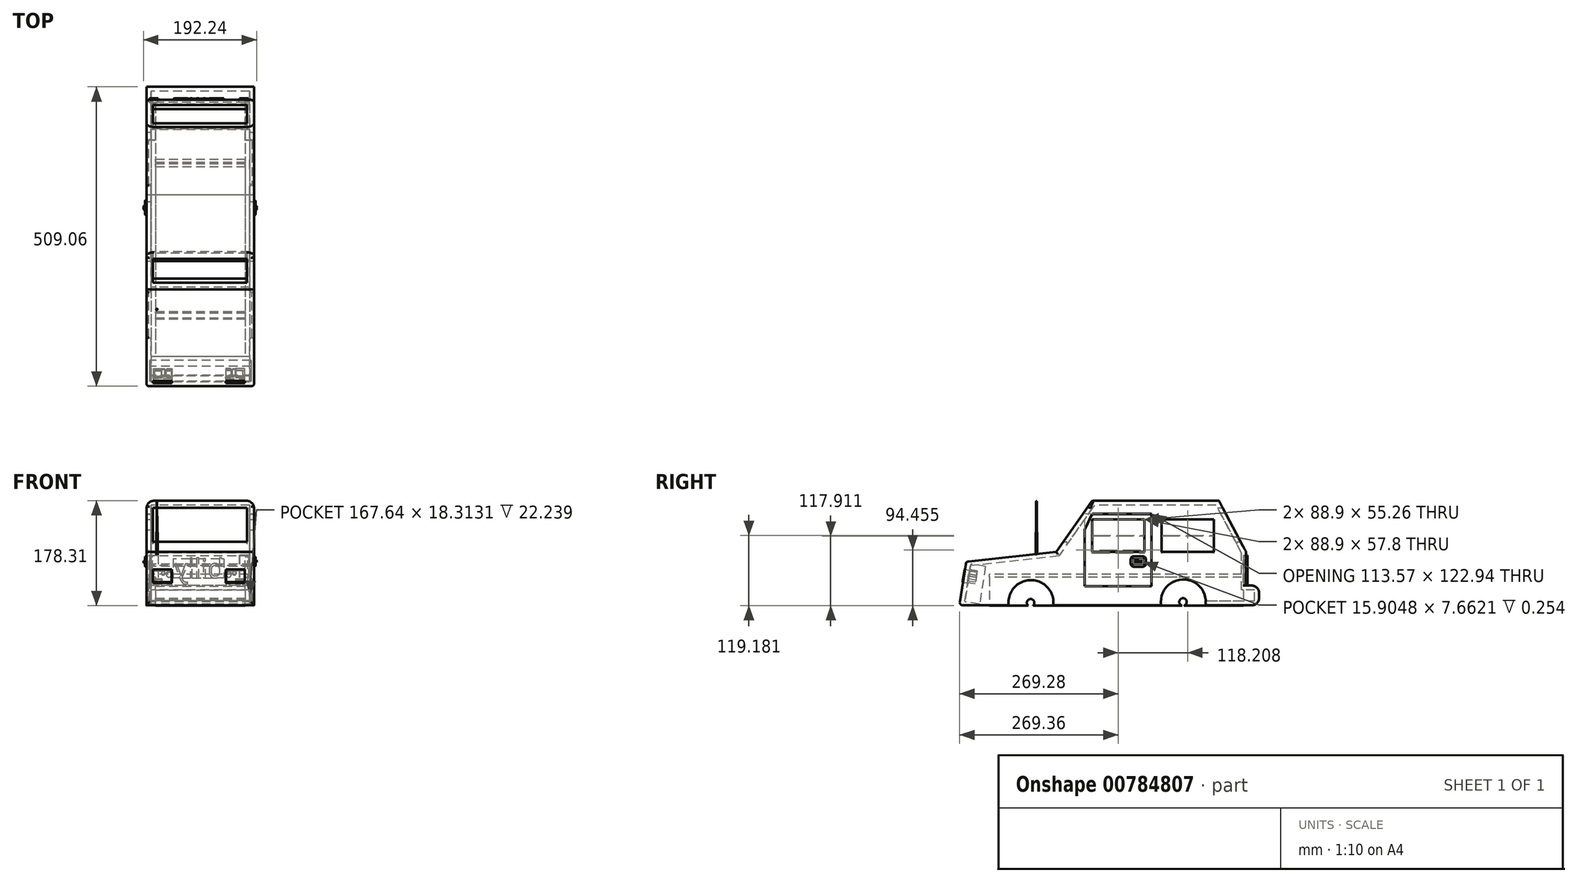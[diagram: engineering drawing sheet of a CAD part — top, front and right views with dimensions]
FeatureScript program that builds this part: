
annotation { "Feature Type Name" : "Feature", "Feature Type Description" : "" }
export const myFeature = defineFeature(function(context is Context, id is Id, definition is map)
    precondition{}
    {
        {
            var Q0;
            Q0=qCreatedBy(makeId("Right.planeOp"),FACE);
            var sketch = newSketch(context, id + "F0", { "sketchPlane" : qUnion([Q0])});
            skLineSegment(sketch, "E0", {"start": v(-225.77, -91.04) * mm, "end": v(261.9, -91.04) * mm});
            skLineSegment(sketch, "E1", {"start": v(261.9, 0) * mm, "end": v(215.84, 86.76) * mm});
            skLineSegment(sketch, "E2", {"start": v(215.84, 86.76) * mm, "end": v(0, 86.76) * mm});
            skLineSegment(sketch, "E3", {"start": v(0, 86.76) * mm, "end": v(-60.74, 0) * mm});
            skLineSegment(sketch, "E4", {"start": v(-60.74, 0) * mm, "end": v(-214.13, -17) * mm});
            skLineSegment(sketch, "E5", {"start": v(-214.13, -17) * mm, "end": v(-225.77, -91.04) * mm});
            skLineSegment(sketch, "E6", {"start": v(261.9, -91.04) * mm, "end": v(261.9, -183.2) * mm});
            skLineSegment(sketch, "E7", {"start": v(261.9, -183.2) * mm, "end": v(139.99, -183.2) * mm});
            skLineSegment(sketch, "E8", {"start": v(-225.77, -91.04) * mm, "end": v(-225.77, -187.69) * mm});
            skLineSegment(sketch, "E9", {"start": v(-225.77, -187.69) * mm, "end": v(-103.85, -187.69) * mm});
            skCircle(sketch, "E10", {"center": v(-103.85, -86.57) * mm, "radius": 38.1 * mm});
            skCircle(sketch, "E11", {"center": v(155.31, -85.2) * mm, "radius": 38.1 * mm});
            skLineSegment(sketch, "E12", {"start": v(261.9, -91.04) * mm, "end": v(284.15, -91.04) * mm});
            skLineSegment(sketch, "E13", {"start": v(284.15, -91.04) * mm, "end": v(284.15, -57.49) * mm});
            skLineSegment(sketch, "E14", {"start": v(284.15, -57.49) * mm, "end": v(261.9, -57.49) * mm});
            skLineSegment(sketch, "E15", {"start": v(261.9, -57.49) * mm, "end": v(261.9, 0) * mm});
            skCircle(sketch, "E16", {"center": v(-103.85, -86.57) * mm, "radius": 6.35 * mm});
            skCircle(sketch, "E17", {"center": v(155.31, -85.2) * mm, "radius": 6.35 * mm});
            skSolve(sketch);
        }
        {
            var Q0;
            Q0=makeQuery(id+"F0.imprint","IMPRINT",FACE,{"disambiguationData":[TD([[makeQuery(id+"F0.imprint","IMPRINT",EDGE,{"derivedFrom":sQuery(id+"F0.wireOp",EDGE,"E1")}),1.0]])]});
            extrude(context, id + "F1", {"entities" : qUnion([Q0]), "depth" : 182.88 * mm, "offsetDistance" : 25.4 * mm});
        }
        {
            var Q0;
            Q0=makeQuery(id+"F1.opExtrude","SWEPT_BODY",BODY,{"disambiguationData":[OSD([sQuery(id+"F0.wireOp",EDGE,"E0"),sQuery(id+"F0.wireOp",EDGE,"QMBNyazt-kVT2-uFLO-qqQZ-oCFPkPWxmDB5"),sQuery(id+"F0.wireOp",EDGE,"E1"),sQuery(id+"F0.wireOp",EDGE,"E2"),sQuery(id+"F0.wireOp",EDGE,"E3"),sQuery(id+"F0.wireOp",EDGE,"E4"),sQuery(id+"F0.wireOp",EDGE,"E5"),sQuery(id+"F0.wireOp",EDGE,"E10"),sQuery(id+"F0.wireOp",EDGE,"E11")])]});
            transform(context, id + "F2", {"entities" : qUnion([Q0]), "transformType" : TransformType.TRANSLATION_3D, "dx" : -88.9 * mm, "dy" : 0 * mm, "dz" : 0 * mm, "makeCopy" : false});
        }
        {
            var Q0;
            {var subQ0=sQuery(id+"F0.wireOp",EDGE,"E0");Q0=makeQuery(id+"F1.opExtrude","SWEPT_FACE",FACE,{"disambiguationData":[OSD([subQ0]),TDD([makeQuery(id+"F0.imprint","IMPRINT",EDGE,{"disambiguationData":[TD([[makeQuery(id+"F0.imprint","INTERSECT",VERTEX,{"disambiguationData":[OD(1.0)],"derivedFrom":[subQ0,sQuery(id+"F0.wireOp",EDGE,"E10")]}),-1.0]])],"derivedFrom":subQ0})])]});}
            var Q1;
            {var subQ0=sQuery(id+"F0.wireOp",EDGE,"E0");Q1=makeQuery(id+"F1.opExtrude","SWEPT_FACE",FACE,{"disambiguationData":[OSD([subQ0]),TDD([makeQuery(id+"F0.imprint","IMPRINT",EDGE,{"disambiguationData":[TD([[makeQuery(id+"F0.imprint","INTERSECT",VERTEX,{"derivedFrom":[subQ0,sQuery(id+"F0.wireOp",EDGE,"QMBNyazt-kVT2-uFLO-qqQZ-oCFPkPWxmDB5")]}),1.0]])],"derivedFrom":subQ0})])]});}
            var Q2;
            {var subQ0=sQuery(id+"F0.wireOp",EDGE,"E0");Q2=makeQuery(id+"F1.opExtrude","SWEPT_FACE",FACE,{"disambiguationData":[OSD([subQ0]),TDD([makeQuery(id+"F0.imprint","IMPRINT",EDGE,{"disambiguationData":[TD([[makeQuery(id+"F0.imprint","INTERSECT",VERTEX,{"derivedFrom":[subQ0,sQuery(id+"F0.wireOp",EDGE,"E5")]}),-1.0]])],"derivedFrom":subQ0})])]});}
            var Q3;
            Q3=makeQuery(id+"F1.opExtrude","SWEPT_FACE",FACE,{"disambiguationData":[OSD([sQuery(id+"F0.wireOp",EDGE,"E10")])]});
            var Q4;
            Q4=makeQuery(id+"F1.opExtrude","SWEPT_FACE",FACE,{"disambiguationData":[OSD([sQuery(id+"F0.wireOp",EDGE,"E11")])]});
            shell(context, id + "F3", {"entities" : qUnion([Q0, Q1, Q2, Q3, Q4]), "thickness" : 7.62 * mm});
        }
        {
            var Q0;
            Q0=makeQuery(id+"F1.opExtrude","CAP_EDGE",EDGE,{"disambiguationData":[OSD([sQuery(id+"F0.wireOp",EDGE,"E2")])],"isStart":false});
            var Q1;
            Q1=makeQuery(id+"F1.opExtrude","CAP_EDGE",EDGE,{"disambiguationData":[OSD([sQuery(id+"F0.wireOp",EDGE,"E2")])],"isStart":true});
            var Q2;
            Q2=makeQuery(id+"F1.opExtrude","SWEPT_EDGE",EDGE,{"disambiguationData":[OSD([sQuery(id+"F0.wireOp",EDGE,"E13"),sQuery(id+"F0.wireOp",EDGE,"E14")])]});
            var Q3;
            Q3=makeQuery(id+"F1.opExtrude","SWEPT_EDGE",EDGE,{"disambiguationData":[OSD([sQuery(id+"F0.wireOp",EDGE,"E12"),sQuery(id+"F0.wireOp",EDGE,"E13")])]});
            fillet(context, id + "F4", {"entities" : qUnion([Q0, Q1, Q2, Q3]), "radius" : 12.7 * mm, "tangentPropagation" : true, "allowEdgeOverflow" : false});
        }
        {
            var Q0;
            Q0=makeQuery(id+"F1.opExtrude","CAP_FACE",FACE,{"disambiguationData":[OSD([sQuery(id+"F0.wireOp",EDGE,"E0"),sQuery(id+"F0.wireOp",EDGE,"QMBNyazt-kVT2-uFLO-qqQZ-oCFPkPWxmDB5"),sQuery(id+"F0.wireOp",EDGE,"E1"),sQuery(id+"F0.wireOp",EDGE,"E2"),sQuery(id+"F0.wireOp",EDGE,"E3"),sQuery(id+"F0.wireOp",EDGE,"E4"),sQuery(id+"F0.wireOp",EDGE,"E5"),sQuery(id+"F0.wireOp",EDGE,"E10"),sQuery(id+"F0.wireOp",EDGE,"E11")])],"isStart":false});
            var sketch = newSketch(context, id + "F5", { "sketchPlane" : qUnion([Q0])});
            skLineSegment(sketch, "E18.bottom", {"start": v(0, 55.26) * mm, "end": v(88.9, 55.26) * mm});
            skLineSegment(sketch, "E18.top", {"start": v(0, 0) * mm, "end": v(88.9, 0) * mm});
            skLineSegment(sketch, "E18.left", {"start": v(0, 55.26) * mm, "end": v(0, 0) * mm});
            skLineSegment(sketch, "E18.right", {"start": v(88.9, 55.26) * mm, "end": v(88.9, 0) * mm});
            skLineSegment(sketch, "E19.bottom", {"start": v(207.1, 55.26) * mm, "end": v(118.2, 55.26) * mm});
            skLineSegment(sketch, "E19.top", {"start": v(207.1, 0) * mm, "end": v(118.2, 0) * mm});
            skLineSegment(sketch, "E19.left", {"start": v(207.1, 55.26) * mm, "end": v(207.1, 0) * mm});
            skLineSegment(sketch, "E19.right", {"start": v(118.2, 55.26) * mm, "end": v(118.2, 0) * mm});
            skSolve(sketch);
        }
        {
            var Q0;
            Q0 = qSketchRegion(id + "F5", true);
            extrude(context, id + "F6", {"entities" : qUnion([Q0]), "operationType" : NewBodyOperationType.REMOVE, "oppositeDirection" : true, "depth" : 182.88 * mm, "offsetDistance" : 25.4 * mm});
        }
        {
            var Q0;
            Q0=makeQuery(id+"F1.opExtrude","SWEPT_FACE",FACE,{"disambiguationData":[OSD([sQuery(id+"F0.wireOp",EDGE,"E15")])]});
            var sketch = newSketch(context, id + "F7", { "sketchPlane" : qUnion([Q0])});
            skLineSegment(sketch, "E20.bottom", {"start": v(-82.2, 74.99) * mm, "end": v(77.83, 74.99) * mm});
            skLineSegment(sketch, "E20.top", {"start": v(-82.2, 16.87) * mm, "end": v(77.83, 16.87) * mm});
            skLineSegment(sketch, "E20.left", {"start": v(-82.2, 74.99) * mm, "end": v(-82.2, 16.87) * mm});
            skLineSegment(sketch, "E20.right", {"start": v(77.83, 74.99) * mm, "end": v(77.83, 16.87) * mm});
            skSolve(sketch);
        }
        {
            var Q0;
            Q0 = qSketchRegion(id + "F7", true);
            extrude(context, id + "F8", {"entities" : qUnion([Q0]), "operationType" : NewBodyOperationType.REMOVE, "oppositeDirection" : true, "depth" : 487.68 * mm, "offsetDistance" : 25.4 * mm});
        }
        {
            var Q0;
            Q0=makeQuery(id+"F1.opExtrude","CAP_EDGE",EDGE,{"disambiguationData":[OSD([sQuery(id+"F0.wireOp",EDGE,"E4")])],"isStart":false});
            var Q1;
            Q1=makeQuery(id+"F1.opExtrude","CAP_EDGE",EDGE,{"disambiguationData":[OSD([sQuery(id+"F0.wireOp",EDGE,"E3")])],"isStart":false});
            var Q2;
            Q2=makeQuery(id+"F1.opExtrude","CAP_EDGE",EDGE,{"disambiguationData":[OSD([sQuery(id+"F0.wireOp",EDGE,"E4")])],"isStart":true});
            var Q3;
            Q3=makeQuery(id+"F1.opExtrude","SWEPT_EDGE",EDGE,{"disambiguationData":[OSD([sQuery(id+"F0.wireOp",EDGE,"E4"),sQuery(id+"F0.wireOp",EDGE,"E5")])]});
            var Q4;
            Q4=makeQuery(id+"F1.opExtrude","CAP_EDGE",EDGE,{"disambiguationData":[OSD([sQuery(id+"F0.wireOp",EDGE,"E5")])],"isStart":true});
            var Q5;
            Q5=makeQuery(id+"F1.opExtrude","SWEPT_EDGE",EDGE,{"disambiguationData":[OSD([sQuery(id+"F0.wireOp",EDGE,"E0"),sQuery(id+"F0.wireOp",EDGE,"E5")])]});
            var Q6;
            Q6=makeQuery(id+"F1.opExtrude","CAP_EDGE",EDGE,{"disambiguationData":[OSD([sQuery(id+"F0.wireOp",EDGE,"E5")])],"isStart":false});
            fillet(context, id + "F9", {"entities" : qUnion([Q0, Q1, Q2, Q3, Q4, Q5, Q6]), "radius" : 5.08 * mm, "tangentPropagation" : true, "allowEdgeOverflow" : false});
        }
        {
            var Q0;
            Q0=makeQuery(id+"F1.opExtrude","SWEPT_EDGE",EDGE,{"disambiguationData":[OSD([sQuery(id+"F0.wireOp",EDGE,"E1"),sQuery(id+"F0.wireOp",EDGE,"E15")])]});
            var Q1;
            Q1=makeQuery(id+"F1.opExtrude","CAP_EDGE",EDGE,{"disambiguationData":[OSD([sQuery(id+"F0.wireOp",EDGE,"E15")])],"isStart":false});
            var Q2;
            Q2=makeQuery(id+"F1.opExtrude","CAP_EDGE",EDGE,{"disambiguationData":[OSD([sQuery(id+"F0.wireOp",EDGE,"E15")])],"isStart":true});
            var Q3;
            Q3=makeQuery(id+"F1.opExtrude","CAP_EDGE",EDGE,{"disambiguationData":[OSD([sQuery(id+"F0.wireOp",EDGE,"E11")])],"isStart":true});
            var Q4;
            {var subQ0=sQuery(id+"F0.wireOp",EDGE,"E11");Q4=makeQuery(id+"F3.opShell","OFFSET_EDGE",EDGE,{"disambiguationData":[OSD([subQ0]),TDD([makeQuery(id+"F1.opExtrude","CAP_EDGE",EDGE,{"disambiguationData":[OSD([subQ0])],"isStart":true})])]});}
            var Q5;
            Q5=makeQuery(id+"F1.opExtrude","CAP_EDGE",EDGE,{"disambiguationData":[OSD([sQuery(id+"F0.wireOp",EDGE,"E10")])],"isStart":true});
            var Q6;
            {var subQ0=sQuery(id+"F0.wireOp",EDGE,"E10");Q6=makeQuery(id+"F3.opShell","OFFSET_EDGE",EDGE,{"disambiguationData":[OSD([subQ0]),TDD([makeQuery(id+"F1.opExtrude","CAP_EDGE",EDGE,{"disambiguationData":[OSD([subQ0])],"isStart":true})])]});}
            var Q7;
            {var subQ0=sQuery(id+"F0.wireOp",EDGE,"E10");Q7=makeQuery(id+"F3.opShell","OFFSET_EDGE",EDGE,{"disambiguationData":[OSD([subQ0]),TDD([makeQuery(id+"F1.opExtrude","CAP_EDGE",EDGE,{"disambiguationData":[OSD([subQ0])],"isStart":false})])]});}
            var Q8;
            Q8=makeQuery(id+"F1.opExtrude","CAP_EDGE",EDGE,{"disambiguationData":[OSD([sQuery(id+"F0.wireOp",EDGE,"E10")])],"isStart":false});
            var Q9;
            Q9=makeQuery(id+"F1.opExtrude","CAP_EDGE",EDGE,{"disambiguationData":[OSD([sQuery(id+"F0.wireOp",EDGE,"E11")])],"isStart":false});
            var Q10;
            {var subQ0=sQuery(id+"F0.wireOp",EDGE,"E11");Q10=makeQuery(id+"F3.opShell","OFFSET_EDGE",EDGE,{"disambiguationData":[OSD([subQ0]),TDD([makeQuery(id+"F1.opExtrude","CAP_EDGE",EDGE,{"disambiguationData":[OSD([subQ0])],"isStart":false})])]});}
            fillet(context, id + "F10", {"entities" : qUnion([Q0, Q1, Q2, Q3, Q4, Q5, Q6, Q7, Q8, Q9, Q10]), "radius" : 5.08 * mm, "tangentPropagation" : true, "allowEdgeOverflow" : false});
        }
        {
            var Q0;
            Q0=makeQuery(id+"F1.opExtrude","SWEPT_FACE",FACE,{"disambiguationData":[OSD([sQuery(id+"F0.wireOp",EDGE,"E2")])]});
            var sketch = newSketch(context, id + "F11", { "sketchPlane" : qUnion([Q0])});
            skLineSegment(sketch, "E21.bottom", {"start": v(-72.8, 259.2) * mm, "end": v(79.6, 259.2) * mm});
            skLineSegment(sketch, "E21.top", {"start": v(-72.8, -172.6) * mm, "end": v(79.6, -172.6) * mm});
            skLineSegment(sketch, "E21.left", {"start": v(-72.8, 259.2) * mm, "end": v(-72.8, -172.6) * mm});
            skLineSegment(sketch, "E21.right", {"start": v(79.6, 259.2) * mm, "end": v(79.6, -172.6) * mm});
            skSolve(sketch);
        }
        {
            var Q0;
            Q0 = qSketchRegion(id + "F11", true);
            extrude(context, id + "F12", {"entities" : qUnion([Q0]), "depth" : 48.26 * mm, "offsetDistance" : 25.4 * mm});
        }
        {
            var Q0;
            Q0=makeQuery(id+"F12.opExtrude","SWEPT_BODY",BODY,{"disambiguationData":[OSD([sQuery(id+"F11.wireOp",EDGE,"E21.bottom"),sQuery(id+"F11.wireOp",EDGE,"E21.top"),sQuery(id+"F11.wireOp",EDGE,"E21.left"),sQuery(id+"F11.wireOp",EDGE,"E21.right")])]});
            transform(context, id + "F13", {"entities" : qUnion([Q0]), "transformType" : TransformType.TRANSLATION_3D, "dx" : -0.76 * mm, "dy" : -1.78 * mm, "dz" : -178.3 * mm, "makeCopy" : false});
        }
        {
            var Q0;
            Q0=makeQuery(id+"F12.opExtrude","SWEPT_FACE",FACE,{"disambiguationData":[OSD([sQuery(id+"F11.wireOp",EDGE,"E21.right")])]});
            var sketch = newSketch(context, id + "F14", { "sketchPlane" : qUnion([Q0])});
            skCircle(sketch, "E22", {"center": v(-104.4, -86.72) * mm, "radius": 6.35 * mm});
            skCircle(sketch, "E23", {"center": v(154.77, -85.35) * mm, "radius": 6.35 * mm});
            skSolve(sketch);
        }
        {
            var Q0;
            Q0 = qSketchRegion(id + "F14", true);
            extrude(context, id + "F15", {"entities" : qUnion([Q0]), "operationType" : NewBodyOperationType.REMOVE, "oppositeDirection" : true, "depth" : 154.94 * mm, "offsetDistance" : 25.4 * mm});
        }
        {
            var Q0;
            Q0=makeQuery(id+"F1.opExtrude","CAP_FACE",FACE,{"disambiguationData":[OSD([sQuery(id+"F0.wireOp",EDGE,"E0"),sQuery(id+"F0.wireOp",EDGE,"E1"),sQuery(id+"F0.wireOp",EDGE,"E2"),sQuery(id+"F0.wireOp",EDGE,"E3"),sQuery(id+"F0.wireOp",EDGE,"E4"),sQuery(id+"F0.wireOp",EDGE,"E5"),sQuery(id+"F0.wireOp",EDGE,"E10"),sQuery(id+"F0.wireOp",EDGE,"E11"),sQuery(id+"F0.wireOp",EDGE,"E12"),sQuery(id+"F0.wireOp",EDGE,"E13"),sQuery(id+"F0.wireOp",EDGE,"E14"),sQuery(id+"F0.wireOp",EDGE,"E15")])],"isStart":false});
            var sketch = newSketch(context, id + "F16", { "sketchPlane" : qUnion([Q0])});
            skLineSegment(sketch, "E24", {"start": v(101.15, 64.38) * mm, "end": v(0, 64.38) * mm});
            skLineSegment(sketch, "E25", {"start": v(101.15, 64.38) * mm, "end": v(101.15, -58.57) * mm});
            skLineSegment(sketch, "E26", {"start": v(101.15, -58.57) * mm, "end": v(-12.41, -58.57) * mm});
            skLineSegment(sketch, "E27", {"start": v(-12.41, -58.57) * mm, "end": v(-12.41, 37.02) * mm});
            skLineSegment(sketch, "E28", {"start": v(-12.41, 37.02) * mm, "end": v(0, 64.38) * mm});
            skPoint(sketch, "E29.endSnap0", {"position": v(118.2, 27.63) * mm});
            skPoint(sketch, "E30", {"position": v(88.9, 27.63) * mm});
            skLineSegment(sketch, "E31", {"start": v(100.88, -58.3) * mm, "end": v(-12.3, -58.3) * mm});
            skLineSegment(sketch, "E32", {"start": v(-12.3, -58.3) * mm, "end": v(-12.3, 37) * mm});
            skLineSegment(sketch, "E33", {"start": v(-12.3, 37) * mm, "end": v(0.08, 64.26) * mm});
            skLineSegment(sketch, "E34", {"start": v(0.08, 64.26) * mm, "end": v(101.02, 64.26) * mm});
            skLineSegment(sketch, "E35", {"start": v(101.02, 64.26) * mm, "end": v(100.88, -58.3) * mm});
            skSolve(sketch);
        }
        {
            var Q0;
            Q0=makeQuery(id+"F12.opExtrude","CAP_FACE",FACE,{"disambiguationData":[OSD([sQuery(id+"F11.wireOp",EDGE,"E21.bottom"),sQuery(id+"F11.wireOp",EDGE,"E21.top"),sQuery(id+"F11.wireOp",EDGE,"E21.left"),sQuery(id+"F11.wireOp",EDGE,"E21.right")])],"isStart":false});
            var sketch = newSketch(context, id + "F17", { "sketchPlane" : qUnion([Q0])});
            skLineSegment(sketch, "E36.bottom", {"start": v(-83.73, 257.43) * mm, "end": v(91.53, 257.43) * mm});
            skLineSegment(sketch, "E36.top", {"start": v(-83.73, -174.37) * mm, "end": v(91.53, -174.37) * mm});
            skLineSegment(sketch, "E36.left", {"start": v(-83.73, 257.43) * mm, "end": v(-83.73, -174.37) * mm});
            skLineSegment(sketch, "E37", {"start": v(91.53, 257.43) * mm, "end": v(91.53, -174.37) * mm});
            skSolve(sketch);
        }
        {
            var Q0;
            Q0 = qSketchRegion(id + "F17", true);
            extrude(context, id + "F18", {"entities" : qUnion([Q0]), "operationType" : NewBodyOperationType.ADD, "depth" : 5.08 * mm, "offsetDistance" : 25.4 * mm});
        }
        {
            var Q0;
            Q0=qCreatedBy(makeId("Top.planeOp"),FACE);
            var sketch = newSketch(context, id + "F19", { "sketchPlane" : qUnion([Q0])});
            skCircle(sketch, "E38", {"center": v(-71.2, -94.38) * mm, "radius": 1.14 * mm});
            skSolve(sketch);
        }
        {
            var Q0;
            Q0 = qSketchRegion(id + "F19", true);
            extrude(context, id + "F20", {"entities" : qUnion([Q0]), "depth" : 38.1 * mm, "offsetDistance" : 25.4 * mm});
        }
        {
            var Q0;
            Q0=makeQuery(id+"F20.opExtrude","SWEPT_BODY",BODY,{"disambiguationData":[OSD([sQuery(id+"F19.wireOp",EDGE,"E38")])]});
            transform(context, id + "F21", {"entities" : qUnion([Q0]), "transformType" : TransformType.TRANSLATION_3D, "dx" : 0 * mm, "dy" : 0 * mm, "dz" : -5.08 * mm, "makeCopy" : false});
        }
        {
            var Q0;
            Q0=makeQuery(id+"F20.opExtrude","CAP_FACE",FACE,{"disambiguationData":[OSD([sQuery(id+"F19.wireOp",EDGE,"E38")])],"isStart":false});
            var sketch = newSketch(context, id + "F22", { "sketchPlane" : qUnion([Q0])});
            skCircle(sketch, "E39", {"center": v(-71.2, -94.38) * mm, "radius": 0.76 * mm});
            skSolve(sketch);
        }
        {
            var Q0;
            Q0 = qSketchRegion(id + "F22", true);
            extrude(context, id + "F23", {"entities" : qUnion([Q0]), "operationType" : NewBodyOperationType.ADD, "depth" : 27.7 * mm, "offsetDistance" : 25.4 * mm});
        }
        {
            var Q0;
            Q0=makeQuery(id+"F23.opExtrude","CAP_FACE",FACE,{"disambiguationData":[OSD([sQuery(id+"F22.wireOp",EDGE,"E39")])],"isStart":false});
            var sketch = newSketch(context, id + "F24", { "sketchPlane" : qUnion([Q0])});
            skCircle(sketch, "E40", {"center": v(-71.2, -94.38) * mm, "radius": 0.45 * mm});
            skSolve(sketch);
        }
        {
            var Q0;
            Q0 = qSketchRegion(id + "F24", true);
            extrude(context, id + "F25", {"entities" : qUnion([Q0]), "operationType" : NewBodyOperationType.ADD, "depth" : 25.4 * mm, "offsetDistance" : 25.4 * mm});
        }
        {
            var Q0;
            Q0 = qSketchRegion(id + "F16", true);
            extrude(context, id + "F26", {"entities" : qUnion([Q0]), "operationType" : NewBodyOperationType.REMOVE, "oppositeDirection" : true, "depth" : 185.42 * mm, "offsetDistance" : 25.4 * mm});
        }
        {
            var Q0;
            {var subQ0=sQuery(id+"F0.wireOp",EDGE,"E15");var subQ1=sQuery(id+"F0.wireOp",EDGE,"E14");var subQ2=sQuery(id+"F0.wireOp",EDGE,"E13");var subQ3=sQuery(id+"F0.wireOp",EDGE,"E12");var subQ4=sQuery(id+"F0.wireOp",EDGE,"E11");var subQ5=sQuery(id+"F0.wireOp",EDGE,"E10");var subQ6=sQuery(id+"F0.wireOp",EDGE,"E5");var subQ7=sQuery(id+"F0.wireOp",EDGE,"E4");var subQ8=sQuery(id+"F0.wireOp",EDGE,"E3");var subQ9=sQuery(id+"F0.wireOp",EDGE,"E2");var subQ10=sQuery(id+"F0.wireOp",EDGE,"E1");var subQ11=sQuery(id+"F0.wireOp",EDGE,"E0");var subQ12=makeQuery(id+"F1.opExtrude","CAP_FACE",FACE,{"disambiguationData":[OSD([subQ11,subQ10,subQ9,subQ8,subQ7,subQ6,subQ5,subQ4,subQ3,subQ2,subQ1,subQ0])],"isStart":false});Q0=makeQuery(id+"F26.boolean.opBoolean","SPLIT",FACE,{"disambiguationData":[TD([makeQuery(id+"F26.opExtrude","SWEPT_FACE",FACE,{"disambiguationData":[OSD([sQuery(id+"F16.wireOp",EDGE,"E31")])]})])],"derivedFrom":subQ12});}
            var sketch = newSketch(context, id + "F27", { "sketchPlane" : qUnion([Q0])});
            skLineSegment(sketch, "E41", {"start": v(27.11, -12.7) * mm, "end": v(27.11, -20.37) * mm});
            skLineSegment(sketch, "E42", {"start": v(70.73, -7.8) * mm, "end": v(86.64, -7.8) * mm});
            skLineSegment(sketch, "E43", {"start": v(70.73, -25.3) * mm, "end": v(86.64, -25.3) * mm});
            skLineSegment(sketch, "E44", {"start": v(30.88, -12.7) * mm, "end": v(30.88, -20.37) * mm});
            skLineSegment(sketch, "E45", {"start": v(70.73, -12.7) * mm, "end": v(70.73, -20.37) * mm});
            skLineSegment(sketch, "E46", {"start": v(86.64, -12.7) * mm, "end": v(86.64, -20.37) * mm});
            skArc(sketch, "E47", {"start": v(70.73, -7.8) * mm, "mid": v(67.27, -9.24) * mm, "end": v(65.83, -12.7) * mm});
            skArc(sketch, "E48", {"start": v(70.73, -25.3) * mm, "mid": v(67.25, -23.85) * mm, "end": v(65.8, -20.37) * mm});
            skArc(sketch, "E49", {"start": v(86.64, -25.3) * mm, "mid": v(90.12, -23.85) * mm, "end": v(91.56, -20.37) * mm});
            skArc(sketch, "E50", {"start": v(86.64, -7.8) * mm, "mid": v(90.1, -9.24) * mm, "end": v(91.54, -12.7) * mm});
            skLineSegment(sketch, "E51", {"start": v(65.83, -12.7) * mm, "end": v(65.8, -20.37) * mm});
            skLineSegment(sketch, "E52", {"start": v(91.54, -12.7) * mm, "end": v(91.56, -20.37) * mm});
            skLineSegment(sketch, "E53", {"start": v(70.73, -20.37) * mm, "end": v(86.64, -20.37) * mm});
            skLineSegment(sketch, "E54", {"start": v(70.73, -12.7) * mm, "end": v(86.64, -12.7) * mm});
            skSolve(sketch);
        }
        {
            var Q0;
            Q0 = qSketchRegion(id + "F27", true);
            extrude(context, id + "F28", {"entities" : qUnion([Q0]), "operationType" : NewBodyOperationType.ADD, "depth" : 2.54 * mm, "offsetDistance" : 25.4 * mm});
        }
        {
            var Q0;
            Q0=makeQuery(id+"F28.opExtrude","CAP_FACE",FACE,{"disambiguationData":[OSD([sQuery(id+"F27.wireOp",EDGE,"E42"),sQuery(id+"F27.wireOp",EDGE,"E43"),sQuery(id+"F27.wireOp",EDGE,"E45"),sQuery(id+"F27.wireOp",EDGE,"E46"),sQuery(id+"F27.wireOp",EDGE,"E47"),sQuery(id+"F27.wireOp",EDGE,"E48"),sQuery(id+"F27.wireOp",EDGE,"E49"),sQuery(id+"F27.wireOp",EDGE,"E50"),sQuery(id+"F27.wireOp",EDGE,"E51"),sQuery(id+"F27.wireOp",EDGE,"E52"),sQuery(id+"F27.wireOp",EDGE,"E53"),sQuery(id+"F27.wireOp",EDGE,"E54")])],"isStart":false});
            var Q1;
            Q1=makeQuery(id+"F28.opExtrude","CAP_EDGE",EDGE,{"disambiguationData":[OSD([sQuery(id+"F27.wireOp",EDGE,"E43")])],"isStart":false});
            var Q2;
            Q2=makeQuery(id+"F28.opExtrude","CAP_EDGE",EDGE,{"disambiguationData":[OSD([sQuery(id+"F27.wireOp",EDGE,"E51")])],"isStart":false});
            var Q3;
            Q3=makeQuery(id+"F28.opExtrude","CAP_EDGE",EDGE,{"disambiguationData":[OSD([sQuery(id+"F27.wireOp",EDGE,"E42")])],"isStart":false});
            var Q4;
            Q4=makeQuery(id+"F28.opExtrude","CAP_EDGE",EDGE,{"disambiguationData":[OSD([sQuery(id+"F27.wireOp",EDGE,"E52")])],"isStart":false});
            var Q5;
            Q5=makeQuery(id+"F28.opExtrude","CAP_EDGE",EDGE,{"disambiguationData":[OSD([sQuery(id+"F27.wireOp",EDGE,"E45")])],"isStart":false});
            var Q6;
            Q6=makeQuery(id+"F28.opExtrude","CAP_EDGE",EDGE,{"disambiguationData":[OSD([sQuery(id+"F27.wireOp",EDGE,"E53")])],"isStart":false});
            var Q7;
            Q7=makeQuery(id+"F28.opExtrude","CAP_EDGE",EDGE,{"disambiguationData":[OSD([sQuery(id+"F27.wireOp",EDGE,"E46")])],"isStart":false});
            var Q8;
            Q8=makeQuery(id+"F28.opExtrude","CAP_EDGE",EDGE,{"disambiguationData":[OSD([sQuery(id+"F27.wireOp",EDGE,"E54")])],"isStart":false});
            fillet(context, id + "F29", {"entities" : qUnion([Q0, Q1, Q2, Q3, Q4, Q5, Q6, Q7, Q8]), "radius" : 2.3 * mm, "tangentPropagation" : true, "allowEdgeOverflow" : false});
        }
        {
            var Q0;
            {var subQ0=sQuery(id+"F11.wireOp",EDGE,"E21.left");var subQ1=sQuery(id+"F11.wireOp",EDGE,"E21.right");Q0=makeQuery(id+"F15.boolean.opBoolean","SPLIT",FACE,{"disambiguationData":[TD([makeQuery(id+"F12.opExtrude","SWEPT_FACE",FACE,{"disambiguationData":[OSD([subQ0])]}),makeQuery(id+"F12.opExtrude","SWEPT_FACE",FACE,{"disambiguationData":[OSD([subQ1])]}),makeQuery(id+"F15.opExtrude","SWEPT_FACE",FACE,{"disambiguationData":[OSD([sQuery(id+"F14.wireOp",EDGE,"E22")])]}),makeQuery(id+"F15.opExtrude","SWEPT_FACE",FACE,{"disambiguationData":[OSD([sQuery(id+"F14.wireOp",EDGE,"E23")])]})])],"derivedFrom":makeQuery(id+"F12.opExtrude","CAP_FACE",FACE,{"disambiguationData":[OSD([sQuery(id+"F11.wireOp",EDGE,"E21.bottom"),sQuery(id+"F11.wireOp",EDGE,"E21.top"),subQ0,subQ1])],"isStart":true})});}
            var sketch = newSketch(context, id + "F30", { "sketchPlane" : qUnion([Q0])});
            skLineSegment(sketch, "E55", {"start": v(94.06, -71.15) * mm, "end": v(98.34, -73.34) * mm});
            skLineSegment(sketch, "E56", {"start": v(98.34, -73.34) * mm, "end": v(98.34, -79.6) * mm});
            skLineSegment(sketch, "E57", {"start": v(98.34, -79.6) * mm, "end": v(94.06, -82.62) * mm});
            skLineSegment(sketch, "E58", {"start": v(94.06, -82.62) * mm, "end": v(94.06, -81.2) * mm});
            skLineSegment(sketch, "E59", {"start": v(94.06, -81.2) * mm, "end": v(97.24, -78.94) * mm});
            skLineSegment(sketch, "E60", {"start": v(97.24, -78.94) * mm, "end": v(97.24, -73.34) * mm});
            skLineSegment(sketch, "E61", {"start": v(97.24, -73.34) * mm, "end": v(94.06, -71.7) * mm});
            skLineSegment(sketch, "E62", {"start": v(94.06, -71.7) * mm, "end": v(94.06, -71.15) * mm});
            skSolve(sketch);
        }
        {
            var Q0;
            Q0 = qSketchRegion(id + "F30", true);
            extrude(context, id + "F31", {"entities" : qUnion([Q0]), "depth" : 3.8 * mm, "offsetDistance" : 25.4 * mm});
        }
        {
            var Q0;
            Q0=makeQuery(id+"F31.opExtrude","SWEPT_BODY",BODY,{"disambiguationData":[OSD([sQuery(id+"F30.wireOp",EDGE,"E55"),sQuery(id+"F30.wireOp",EDGE,"E56"),sQuery(id+"F30.wireOp",EDGE,"E57"),sQuery(id+"F30.wireOp",EDGE,"E58"),sQuery(id+"F30.wireOp",EDGE,"E59"),sQuery(id+"F30.wireOp",EDGE,"E60"),sQuery(id+"F30.wireOp",EDGE,"E61"),sQuery(id+"F30.wireOp",EDGE,"E62")])]});
            transform(context, id + "F32", {"entities" : qUnion([Q0]), "transformType" : TransformType.TRANSLATION_3D, "dx" : 0 * mm, "dy" : 1.61 * mm, "dz" : 77.3 * mm, "makeCopy" : false});
        }
        {
            var Q0;
            {var subQ0=sQuery(id+"F0.wireOp",EDGE,"E15");var subQ1=sQuery(id+"F0.wireOp",EDGE,"E14");var subQ2=sQuery(id+"F0.wireOp",EDGE,"E13");var subQ3=sQuery(id+"F0.wireOp",EDGE,"E12");var subQ4=sQuery(id+"F0.wireOp",EDGE,"E11");var subQ5=sQuery(id+"F0.wireOp",EDGE,"E10");var subQ6=sQuery(id+"F0.wireOp",EDGE,"E5");var subQ7=sQuery(id+"F0.wireOp",EDGE,"E4");var subQ8=sQuery(id+"F0.wireOp",EDGE,"E3");var subQ9=sQuery(id+"F0.wireOp",EDGE,"E2");var subQ10=sQuery(id+"F0.wireOp",EDGE,"E1");var subQ11=sQuery(id+"F0.wireOp",EDGE,"E0");var subQ12=makeQuery(id+"F1.opExtrude","CAP_FACE",FACE,{"disambiguationData":[OSD([subQ11,subQ10,subQ9,subQ8,subQ7,subQ6,subQ5,subQ4,subQ3,subQ2,subQ1,subQ0])],"isStart":true});Q0=makeQuery(id+"F26.boolean.opBoolean","SPLIT",FACE,{"disambiguationData":[TD([makeQuery(id+"F26.opExtrude","SWEPT_FACE",FACE,{"disambiguationData":[OSD([sQuery(id+"F16.wireOp",EDGE,"E31")])]})])],"derivedFrom":subQ12});}
            var sketch = newSketch(context, id + "F33", { "sketchPlane" : qUnion([Q0])});
            skLineSegment(sketch, "E63", {"start": v(32.03, 0) * mm, "end": v(32.03, -20.71) * mm});
            skLineSegment(sketch, "E64", {"start": v(-44.47, -12.93) * mm, "end": v(-44.47, -20.6) * mm});
            skLineSegment(sketch, "E65", {"start": v(-86.62, -8.03) * mm, "end": v(-70.72, -8.03) * mm});
            skLineSegment(sketch, "E66", {"start": v(-86.62, -25.52) * mm, "end": v(-70.72, -25.52) * mm});
            skLineSegment(sketch, "E67", {"start": v(-55.59, -12.93) * mm, "end": v(-55.59, -20.6) * mm});
            skLineSegment(sketch, "E68", {"start": v(-86.62, -12.93) * mm, "end": v(-86.62, -20.6) * mm});
            skLineSegment(sketch, "E69", {"start": v(-70.72, -12.93) * mm, "end": v(-70.72, -20.6) * mm});
            skArc(sketch, "E70", {"start": v(-86.62, -8.03) * mm, "mid": v(-90.09, -9.47) * mm, "end": v(-91.52, -12.93) * mm});
            skArc(sketch, "E71", {"start": v(-86.62, -25.52) * mm, "mid": v(-90.1, -24.08) * mm, "end": v(-91.55, -20.6) * mm});
            skArc(sketch, "E72", {"start": v(-70.72, -25.52) * mm, "mid": v(-67.23, -24.08) * mm, "end": v(-65.79, -20.6) * mm});
            skArc(sketch, "E73", {"start": v(-70.72, -8.03) * mm, "mid": v(-67.25, -9.47) * mm, "end": v(-65.81, -12.93) * mm});
            skLineSegment(sketch, "E74", {"start": v(-91.52, -12.93) * mm, "end": v(-91.55, -20.6) * mm});
            skLineSegment(sketch, "E75", {"start": v(-65.81, -12.93) * mm, "end": v(-65.79, -20.6) * mm});
            skLineSegment(sketch, "E76", {"start": v(-86.62, -20.6) * mm, "end": v(-70.72, -20.6) * mm});
            skLineSegment(sketch, "E77", {"start": v(-86.62, -12.93) * mm, "end": v(-70.72, -12.93) * mm});
            skSolve(sketch);
        }
        {
            var Q0;
            Q0=makeQuery(id+"F33.imprint","IMPRINT",FACE,{"disambiguationData":[TD([[makeQuery(id+"F33.imprint","IMPRINT",EDGE,{"derivedFrom":sQuery(id+"F33.wireOp",EDGE,"E65")}),-1.0]])]});
            extrude(context, id + "F34", {"entities" : qUnion([Q0]), "operationType" : NewBodyOperationType.ADD, "depth" : 2.54 * mm, "offsetDistance" : 25.4 * mm});
        }
        {
            var Q0;
            Q0=makeQuery(id+"F34.opExtrude","CAP_EDGE",EDGE,{"disambiguationData":[OSD([sQuery(id+"F33.wireOp",EDGE,"E77")])],"isStart":false});
            var Q1;
            Q1=makeQuery(id+"F34.opExtrude","CAP_EDGE",EDGE,{"disambiguationData":[OSD([sQuery(id+"F33.wireOp",EDGE,"E68")])],"isStart":false});
            var Q2;
            Q2=makeQuery(id+"F34.opExtrude","CAP_EDGE",EDGE,{"disambiguationData":[OSD([sQuery(id+"F33.wireOp",EDGE,"E76")])],"isStart":false});
            var Q3;
            Q3=makeQuery(id+"F34.opExtrude","CAP_EDGE",EDGE,{"disambiguationData":[OSD([sQuery(id+"F33.wireOp",EDGE,"E69")])],"isStart":false});
            var Q4;
            Q4=makeQuery(id+"F34.opExtrude","CAP_EDGE",EDGE,{"disambiguationData":[OSD([sQuery(id+"F33.wireOp",EDGE,"E72")])],"isStart":false});
            var Q5;
            Q5=makeQuery(id+"F34.opExtrude","CAP_EDGE",EDGE,{"disambiguationData":[OSD([sQuery(id+"F33.wireOp",EDGE,"E71")])],"isStart":false});
            var Q6;
            Q6=makeQuery(id+"F34.opExtrude","CAP_EDGE",EDGE,{"disambiguationData":[OSD([sQuery(id+"F33.wireOp",EDGE,"E70")])],"isStart":false});
            var Q7;
            Q7=makeQuery(id+"F34.opExtrude","CAP_EDGE",EDGE,{"disambiguationData":[OSD([sQuery(id+"F33.wireOp",EDGE,"E73")])],"isStart":false});
            fillet(context, id + "F35", {"entities" : qUnion([Q0, Q1, Q2, Q3, Q4, Q5, Q6, Q7]), "radius" : 1.73 * mm, "tangentPropagation" : true, "allowEdgeOverflow" : false});
        }
        {
            var Q0;
            {var subQ0=sQuery(id+"F11.wireOp",EDGE,"E21.right");var subQ1=sQuery(id+"F11.wireOp",EDGE,"E21.left");var subQ2=makeQuery(id+"F12.opExtrude","CAP_FACE",FACE,{"disambiguationData":[OSD([sQuery(id+"F11.wireOp",EDGE,"E21.bottom"),sQuery(id+"F11.wireOp",EDGE,"E21.top"),subQ1,subQ0])],"isStart":true});var subQ3=makeQuery(id+"F15.opExtrude","SWEPT_FACE",FACE,{"disambiguationData":[OSD([sQuery(id+"F14.wireOp",EDGE,"E22")])]});Q0=makeQuery(id+"F30.imprint","IMPRINT",FACE,{"disambiguationData":[TD([[makeQuery(id+"F30.imprint","IMPRINT",EDGE,{"derivedFrom":makeQuery(id+"F15.boolean.opBoolean","INTERSECT",EDGE,{"disambiguationData":[OD(1.0)],"derivedFrom":[subQ2,subQ3]})}),1.0]])]});}
            var sketch = newSketch(context, id + "F36", { "sketchPlane" : qUnion([Q0])});
            skLineSegment(sketch, "E78", {"start": v(-1.87, 5.34) * mm, "end": v(2.41, 3.15) * mm});
            skLineSegment(sketch, "E79", {"start": v(2.41, 3.15) * mm, "end": v(2.41, -3.11) * mm});
            skLineSegment(sketch, "E80", {"start": v(2.41, -3.11) * mm, "end": v(-1.87, -6.14) * mm});
            skLineSegment(sketch, "E81", {"start": v(-1.87, -6.14) * mm, "end": v(-1.87, -4.7) * mm});
            skLineSegment(sketch, "E82", {"start": v(-1.87, -4.7) * mm, "end": v(1.32, -2.45) * mm});
            skLineSegment(sketch, "E83", {"start": v(1.32, -2.45) * mm, "end": v(1.32, 3.15) * mm});
            skLineSegment(sketch, "E84", {"start": v(1.32, 3.15) * mm, "end": v(-1.87, 4.78) * mm});
            skLineSegment(sketch, "E85", {"start": v(-1.87, 4.78) * mm, "end": v(-1.87, 5.34) * mm});
            skSolve(sketch);
        }
        {
            var Q0;
            Q0 = qSketchRegion(id + "F36", true);
            extrude(context, id + "F37", {"entities" : qUnion([Q0]), "depth" : 3.8 * mm, "offsetDistance" : 25.4 * mm});
        }
        {
            var Q0;
            Q0=makeQuery(id+"F37.opExtrude","SWEPT_BODY",BODY,{"disambiguationData":[OSD([sQuery(id+"F36.wireOp",EDGE,"E78"),sQuery(id+"F36.wireOp",EDGE,"E79"),sQuery(id+"F36.wireOp",EDGE,"E80"),sQuery(id+"F36.wireOp",EDGE,"E81"),sQuery(id+"F36.wireOp",EDGE,"E82"),sQuery(id+"F36.wireOp",EDGE,"E83"),sQuery(id+"F36.wireOp",EDGE,"E84"),sQuery(id+"F36.wireOp",EDGE,"E85")])]});
            var Q1;
            Q1=makeQuery(id+"F37.opExtrude","CAP_EDGE",EDGE,{"disambiguationData":[OSD([sQuery(id+"F36.wireOp",EDGE,"E83")])],"isStart":false});
            transform(context, id + "F38", {"entities" : qUnion([Q0]), "transformType" : TransformType.ROTATION, "transformAxis" : qUnion([Q1]), "angle" : 180 * degree, "makeCopy" : false});
        }
        {
            var Q0;
            Q0=makeQuery(id+"F37.opExtrude","SWEPT_BODY",BODY,{"disambiguationData":[OSD([sQuery(id+"F36.wireOp",EDGE,"E78"),sQuery(id+"F36.wireOp",EDGE,"E79"),sQuery(id+"F36.wireOp",EDGE,"E80"),sQuery(id+"F36.wireOp",EDGE,"E81"),sQuery(id+"F36.wireOp",EDGE,"E82"),sQuery(id+"F36.wireOp",EDGE,"E83"),sQuery(id+"F36.wireOp",EDGE,"E84"),sQuery(id+"F36.wireOp",EDGE,"E85")])]});
            transform(context, id + "F39", {"entities" : qUnion([Q0]), "transformType" : TransformType.TRANSLATION_3D, "dx" : -94.13 * mm, "dy" : 78.38 * mm, "dz" : 79.7 * mm, "makeCopy" : false});
        }
        {
            var Q0;
            Q0=makeQuery(id+"F1.opExtrude","SWEPT_FACE",FACE,{"disambiguationData":[OSD([sQuery(id+"F0.wireOp",EDGE,"E15")])]});
            var sketch = newSketch(context, id + "F40", { "sketchPlane" : qUnion([Q0])});
            skLineSegment(sketch, "E86.bottom", {"start": v(-84.4, -5.9) * mm, "end": v(-68.86, -5.9) * mm});
            skLineSegment(sketch, "E86.top", {"start": v(-84.4, -53.57) * mm, "end": v(-68.86, -53.57) * mm});
            skLineSegment(sketch, "E86.left", {"start": v(-84.4, -5.9) * mm, "end": v(-84.4, -53.57) * mm});
            skLineSegment(sketch, "E86.right", {"start": v(-68.86, -5.9) * mm, "end": v(-68.86, -53.57) * mm});
            skLineSegment(sketch, "E87", {"start": v(0, 0) * mm, "end": v(0, -57.49) * mm});
            skLineSegment(sketch, "E88.MirrorCS", {"start": v(84.4, -53.57) * mm, "end": v(68.86, -53.57) * mm});
            skLineSegment(sketch, "E89.MirrorCS", {"start": v(84.4, -5.9) * mm, "end": v(68.86, -5.9) * mm});
            skLineSegment(sketch, "E90.MirrorCS", {"start": v(68.86, -5.9) * mm, "end": v(68.86, -53.57) * mm});
            skLineSegment(sketch, "E91.MirrorCS", {"start": v(84.4, -5.9) * mm, "end": v(84.4, -53.57) * mm});
            skSolve(sketch);
        }
        {
            var Q0;
            Q0 = qSketchRegion(id + "F40", true);
            extrude(context, id + "F41", {"entities" : qUnion([Q0]), "operationType" : NewBodyOperationType.REMOVE, "oppositeDirection" : true, "depth" : 4.32 * mm, "offsetDistance" : 25.4 * mm});
        }
        {
            var Q0;
            Q0=makeQuery(id+"F41.boolean.opBoolean","COPY",FACE,{"derivedFrom":makeQuery(id+"F41.opExtrude","CAP_FACE",FACE,{"disambiguationData":[OSD([sQuery(id+"F40.wireOp",EDGE,"E86.bottom"),sQuery(id+"F40.wireOp",EDGE,"E86.top"),sQuery(id+"F40.wireOp",EDGE,"E86.left"),sQuery(id+"F40.wireOp",EDGE,"E86.right")])],"isStart":false})});
            var sketch = newSketch(context, id + "F42", { "sketchPlane" : qUnion([Q0])});
            skLineSegment(sketch, "E92.bottom", {"start": v(-83.46, -52.46) * mm, "end": v(-78.87, -52.46) * mm});
            skLineSegment(sketch, "E92.top", {"start": v(-83.46, -8.47) * mm, "end": v(-78.87, -8.47) * mm});
            skLineSegment(sketch, "E92.left", {"start": v(-83.46, -52.46) * mm, "end": v(-83.46, -8.47) * mm});
            skLineSegment(sketch, "E92.right", {"start": v(-78.87, -52.46) * mm, "end": v(-78.87, -8.47) * mm});
            skLineSegment(sketch, "E93.MirrorCS", {"start": v(83.46, -8.47) * mm, "end": v(78.87, -8.47) * mm});
            skLineSegment(sketch, "E94.MirrorCS", {"start": v(78.87, -52.46) * mm, "end": v(78.87, -8.47) * mm});
            skLineSegment(sketch, "E95.MirrorCS", {"start": v(83.46, -52.46) * mm, "end": v(83.46, -8.47) * mm});
            skLineSegment(sketch, "E96.MirrorCS", {"start": v(83.46, -52.46) * mm, "end": v(78.87, -52.46) * mm});
            skSolve(sketch);
        }
        {
            var Q0;
            Q0 = qSketchRegion(id + "F42", true);
            extrude(context, id + "F43", {"entities" : qUnion([Q0]), "depth" : 2.54 * mm, "offsetDistance" : 25.4 * mm});
        }
        {
            var Q0;
            Q0=makeQuery(id+"F43.opExtrude","CAP_EDGE",EDGE,{"disambiguationData":[OSD([sQuery(id+"F42.wireOp",EDGE,"E92.bottom")])],"isStart":false});
            var Q1;
            Q1=makeQuery(id+"F43.opExtrude","CAP_EDGE",EDGE,{"disambiguationData":[OSD([sQuery(id+"F42.wireOp",EDGE,"E96.MirrorCS")])],"isStart":false});
            var Q2;
            Q2=makeQuery(id+"F43.opExtrude","CAP_EDGE",EDGE,{"disambiguationData":[OSD([sQuery(id+"F42.wireOp",EDGE,"E93.MirrorCS")])],"isStart":false});
            var Q3;
            Q3=makeQuery(id+"F43.opExtrude","CAP_EDGE",EDGE,{"disambiguationData":[OSD([sQuery(id+"F42.wireOp",EDGE,"E94.MirrorCS")])],"isStart":false});
            var Q4;
            Q4=makeQuery(id+"F43.opExtrude","CAP_EDGE",EDGE,{"disambiguationData":[OSD([sQuery(id+"F42.wireOp",EDGE,"E92.left")])],"isStart":false});
            var Q5;
            Q5=makeQuery(id+"F43.opExtrude","CAP_EDGE",EDGE,{"disambiguationData":[OSD([sQuery(id+"F42.wireOp",EDGE,"E92.right")])],"isStart":false});
            var Q6;
            Q6=makeQuery(id+"F43.opExtrude","CAP_EDGE",EDGE,{"disambiguationData":[OSD([sQuery(id+"F42.wireOp",EDGE,"E95.MirrorCS")])],"isStart":false});
            var Q7;
            Q7=makeQuery(id+"F43.opExtrude","CAP_EDGE",EDGE,{"disambiguationData":[OSD([sQuery(id+"F42.wireOp",EDGE,"E92.top")])],"isStart":false});
            fillet(context, id + "F44", {"entities" : qUnion([Q0, Q1, Q2, Q3, Q4, Q5, Q6, Q7]), "radius" : 1.27 * mm, "tangentPropagation" : true, "allowEdgeOverflow" : false});
        }
        {
            var Q0;
            Q0=makeQuery(id+"F1.opExtrude","SWEPT_FACE",FACE,{"disambiguationData":[OSD([sQuery(id+"F0.wireOp",EDGE,"E15")])]});
            var sketch = newSketch(context, id + "F45", { "sketchPlane" : qUnion([Q0])});
            skLineSegment(sketch, "E97.bottom", {"start": v(-84.86, -5.9) * mm, "end": v(-69.3, -5.9) * mm});
            skLineSegment(sketch, "E97.top", {"start": v(-84.86, -53.57) * mm, "end": v(-69.3, -53.57) * mm});
            skLineSegment(sketch, "E97.left", {"start": v(-84.86, -5.9) * mm, "end": v(-84.86, -53.57) * mm});
            skLineSegment(sketch, "E97.right", {"start": v(-69.3, -5.9) * mm, "end": v(-69.3, -53.57) * mm});
            skLineSegment(sketch, "E98", {"start": v(-0.45, 0) * mm, "end": v(-0.45, -57.48) * mm});
            skLineSegment(sketch, "E99.MirrorCS", {"start": v(83.95, -53.57) * mm, "end": v(68.4, -53.57) * mm});
            skLineSegment(sketch, "E100.MirrorCS", {"start": v(83.95, -5.9) * mm, "end": v(68.4, -5.9) * mm});
            skLineSegment(sketch, "E101.MirrorCS", {"start": v(68.4, -5.9) * mm, "end": v(68.4, -53.57) * mm});
            skLineSegment(sketch, "E102.MirrorCS", {"start": v(83.95, -5.9) * mm, "end": v(83.95, -53.57) * mm});
            skSolve(sketch);
        }
        {
            var Q0;
            {var subQ2=sQuery(id+"F45.wireOp",EDGE,"E102.MirrorCS");Q0=makeQuery(id+"F45.imprint","IMPRINT",FACE,{"disambiguationData":[TD([[makeQuery(id+"F45.imprint","IMPRINT",EDGE,{"derivedFrom":subQ2}),-1.0]])]});}
            var Q1;
            {var subQ0=sQuery(id+"F45.wireOp",EDGE,"E97.right");var subQ1=sQuery(id+"F45.wireOp",EDGE,"E97.top");var subQ2=makeQuery(id+"F45.imprint","INTERSECT",VERTEX,{"derivedFrom":[subQ1,subQ0]});Q1=makeQuery(id+"F45.imprint","IMPRINT",FACE,{"disambiguationData":[TD([[makeQuery(id+"F45.imprint","IMPRINT",EDGE,{"disambiguationData":[TD([[subQ2,1.0]])],"derivedFrom":subQ1}),1.0]])]});}
            var Q2;
            Q2=sQuery(id+"F45.wireOp",EDGE,"E97.right");
            var Q3;
            Q3=sQuery(id+"F45.wireOp",EDGE,"E101.MirrorCS");
            var Q4;
            Q4=sQuery(id+"F45.wireOp",EDGE,"E97.top");
            var Q5;
            Q5=sQuery(id+"F45.wireOp",EDGE,"E102.MirrorCS");
            var Q6;
            Q6=sQuery(id+"F45.wireOp",EDGE,"E99.MirrorCS");
            var Q7;
            Q7=sQuery(id+"F45.wireOp",EDGE,"E97.bottom");
            var Q8;
            Q8=sQuery(id+"F45.wireOp",EDGE,"E98");
            var Q9;
            Q9=sQuery(id+"F45.wireOp",EDGE,"E100.MirrorCS");
            var Q10;
            Q10=sQuery(id+"F45.wireOp",EDGE,"E97.left");
            extrude(context, id + "F46", {"entities" : qUnion([Q0, Q1]), "surfaceEntities" : qUnion([Q2, Q3, Q4, Q5, Q6, Q7, Q8, Q9, Q10]), "depth" : 2.54 * mm, "offsetDistance" : 25.4 * mm});
        }
        {
            var Q0;
            Q0=makeQuery(id+"F1.opExtrude","SWEPT_FACE",FACE,{"disambiguationData":[OSD([sQuery(id+"F0.wireOp",EDGE,"E15")])]});
            var sketch = newSketch(context, id + "F47", { "sketchPlane" : qUnion([Q0])});
            skLineSegment(sketch, "E103.bottom", {"start": v(-42.62, -12.15) * mm, "end": v(44, -12.15) * mm});
            skLineSegment(sketch, "E103.top", {"start": v(-42.62, -44.3) * mm, "end": v(44, -44.3) * mm});
            skLineSegment(sketch, "E103.left", {"start": v(-42.62, -12.15) * mm, "end": v(-42.62, -44.3) * mm});
            skLineSegment(sketch, "E103.right", {"start": v(44, -12.15) * mm, "end": v(44, -44.3) * mm});
            skText(sketch, "E104", { "text": "billy", "fontName": "OpenSans-Regular.ttf"});
            const initialGuessF47  = {"E104": [-0.04262, -0.0443, 1, 0, 0.03216]};
            skSetInitialGuess(sketch, initialGuessF47);
            skSolve(sketch);
        }
        {
            var Q0;
            {var subQ5=sQuery(id+"F47.wireOp",EDGE,"E104.sketch_text.stroke-41");Q0=makeQuery(id+"F47.imprint","IMPRINT",FACE,{"disambiguationData":[TD([[makeQuery(id+"F47.imprint","IMPRINT",EDGE,{"derivedFrom":subQ5}),-1.0]])]});}
            var Q1;
            Q1=makeQuery(id+"F47.imprint","IMPRINT",FACE,{"disambiguationData":[TD([[makeQuery(id+"F47.imprint","IMPRINT",EDGE,{"derivedFrom":sQuery(id+"F47.wireOp",EDGE,"E104.sketch_text.stroke-0")}),-1.0]])]});
            var Q2;
            Q2=makeQuery(id+"F47.imprint","IMPRINT",FACE,{"disambiguationData":[TD([[makeQuery(id+"F47.imprint","IMPRINT",EDGE,{"derivedFrom":sQuery(id+"F47.wireOp",EDGE,"E104.sketch_text.stroke-23")}),-1.0]])]});
            var Q3;
            {var subQ0=sQuery(id+"F47.wireOp",EDGE,"E104.sketch_text.stroke-4");var subQ1=sQuery(id+"F47.wireOp",EDGE,"E103.top");var subQ2=makeQuery(id+"F47.imprint","INTERSECT",VERTEX,{"derivedFrom":[subQ1,subQ0]});Q3=makeQuery(id+"F47.imprint","IMPRINT",FACE,{"disambiguationData":[TD([[makeQuery(id+"F47.imprint","IMPRINT",EDGE,{"disambiguationData":[TD([[subQ2,-1.0]])],"derivedFrom":subQ1}),-1.0]])]});}
            var Q4;
            {var subQ0=sQuery(id+"F47.wireOp",EDGE,"E104.sketch_text.stroke-51");Q4=makeQuery(id+"F47.imprint","IMPRINT",FACE,{"disambiguationData":[TD([[makeQuery(id+"F47.imprint","IMPRINT",EDGE,{"derivedFrom":subQ0}),-1.0]])]});}
            var Q5;
            {var subQ5=sQuery(id+"F47.wireOp",EDGE,"E104.sketch_text.stroke-10");Q5=makeQuery(id+"F47.imprint","IMPRINT",FACE,{"disambiguationData":[TD([[makeQuery(id+"F47.imprint","IMPRINT",EDGE,{"derivedFrom":subQ5}),-1.0]])]});}
            var Q6;
            {var subQ0=sQuery(id+"F47.wireOp",EDGE,"E104.sketch_text.stroke-31");Q6=makeQuery(id+"F47.imprint","IMPRINT",FACE,{"disambiguationData":[TD([[makeQuery(id+"F47.imprint","IMPRINT",EDGE,{"derivedFrom":subQ0}),-1.0]])]});}
            var Q7;
            {var subQ5=sQuery(id+"F47.wireOp",EDGE,"E104.sketch_text.stroke-37");Q7=makeQuery(id+"F47.imprint","IMPRINT",FACE,{"disambiguationData":[TD([[makeQuery(id+"F47.imprint","IMPRINT",EDGE,{"derivedFrom":subQ5}),-1.0]])]});}
            var Q8;
            {var subQ1=sQuery(id+"F47.wireOp",EDGE,"E104.sketch_text.stroke-28");Q8=makeQuery(id+"F47.imprint","IMPRINT",FACE,{"disambiguationData":[TD([[makeQuery(id+"F47.imprint","IMPRINT",EDGE,{"derivedFrom":subQ1}),-1.0]])]});}
            var Q9;
            {var subQ0=sQuery(id+"F47.wireOp",EDGE,"E104.sketch_text.stroke-43");Q9=makeQuery(id+"F47.imprint","IMPRINT",FACE,{"disambiguationData":[TD([[makeQuery(id+"F47.imprint","IMPRINT",EDGE,{"derivedFrom":subQ0}),-1.0]])]});}
            var Q10;
            {var subQ5=sQuery(id+"F47.wireOp",EDGE,"E104.sketch_text.stroke-35");Q10=makeQuery(id+"F47.imprint","IMPRINT",FACE,{"disambiguationData":[TD([[makeQuery(id+"F47.imprint","IMPRINT",EDGE,{"derivedFrom":subQ5}),-1.0]])]});}
            var Q11;
            {var subQ0=sQuery(id+"F47.wireOp",EDGE,"E104.sketch_text.stroke-5");Q11=makeQuery(id+"F47.imprint","IMPRINT",FACE,{"disambiguationData":[TD([[makeQuery(id+"F47.imprint","IMPRINT",EDGE,{"derivedFrom":subQ0}),1.0]])]});}
            var Q12;
            {var subQ5=sQuery(id+"F47.wireOp",EDGE,"E104.sketch_text.stroke-39");Q12=makeQuery(id+"F47.imprint","IMPRINT",FACE,{"disambiguationData":[TD([[makeQuery(id+"F47.imprint","IMPRINT",EDGE,{"derivedFrom":subQ5}),-1.0]])]});}
            extrude(context, id + "F48", {"entities" : qUnion([Q0, Q1, Q2, Q3, Q4, Q5, Q6, Q7, Q8, Q9, Q10, Q11, Q12]), "depth" : 2.54 * mm, "offsetDistance" : 25.4 * mm});
        }
        {
            var Q0;
            Q0 = qSketchRegion(id + "F47", true);
            extrude(context, id + "F49", {"entities" : qUnion([Q0]), "operationType" : NewBodyOperationType.ADD, "depth" : 2.03 * mm, "offsetDistance" : 25.4 * mm});
        }
        {
            var Q0;
            Q0=makeQuery(id+"F1.opExtrude","SWEPT_FACE",FACE,{"disambiguationData":[OSD([sQuery(id+"F0.wireOp",EDGE,"E5")])]});
            var sketch = newSketch(context, id + "F50", { "sketchPlane" : qUnion([Q0])});
            skLineSegment(sketch, "E105.bottom", {"start": v(-83.82, -53.9) * mm, "end": v(88.9, -53.9) * mm});
            skLineSegment(sketch, "E105.top", {"start": v(-83.82, -119.05) * mm, "end": v(88.9, -119.05) * mm});
            skLineSegment(sketch, "E105.left", {"start": v(-83.82, -53.9) * mm, "end": v(-83.82, -119.05) * mm});
            skLineSegment(sketch, "E105.right", {"start": v(88.9, -53.9) * mm, "end": v(88.9, -119.05) * mm});
            skSolve(sketch);
        }
        {
            var Q0;
            Q0 = qSketchRegion(id + "F50", true);
            extrude(context, id + "F51", {"entities" : qUnion([Q0]), "oppositeDirection" : true, "depth" : 25.4 * mm, "offsetDistance" : 25.4 * mm});
        }
        {
            var Q0;
            Q0=makeQuery(id+"F1.opExtrude","SWEPT_FACE",FACE,{"disambiguationData":[OSD([sQuery(id+"F0.wireOp",EDGE,"E5")])]});
            var sketch = newSketch(context, id + "F52", { "sketchPlane" : qUnion([Q0])});
            skLineSegment(sketch, "E106.bottom", {"start": v(-77.37, -63.87) * mm, "end": v(-45.72, -63.87) * mm});
            skLineSegment(sketch, "E106.top", {"start": v(-77.37, -86.07) * mm, "end": v(-45.72, -86.07) * mm});
            skLineSegment(sketch, "E106.left", {"start": v(-77.37, -63.87) * mm, "end": v(-77.37, -86.07) * mm});
            skLineSegment(sketch, "E106.right", {"start": v(-45.72, -63.87) * mm, "end": v(-45.72, -86.07) * mm});
            skLineSegment(sketch, "E107", {"start": v(0, -35.38) * mm, "end": v(0, -119.05) * mm});
            skLineSegment(sketch, "E108.MirrorCS", {"start": v(77.37, -63.87) * mm, "end": v(77.37, -86.07) * mm});
            skLineSegment(sketch, "E109.MirrorCS", {"start": v(45.72, -63.87) * mm, "end": v(45.72, -86.07) * mm});
            skLineSegment(sketch, "E110.MirrorCS", {"start": v(77.37, -63.87) * mm, "end": v(45.72, -63.87) * mm});
            skLineSegment(sketch, "E111.MirrorCS", {"start": v(77.37, -86.07) * mm, "end": v(45.72, -86.07) * mm});
            skSolve(sketch);
        }
        {
            var Q0;
            Q0 = qSketchRegion(id + "F52", true);
            extrude(context, id + "F53", {"entities" : qUnion([Q0]), "operationType" : NewBodyOperationType.REMOVE, "oppositeDirection" : true, "depth" : 12.7 * mm, "offsetDistance" : 25.4 * mm});
        }
        {
            var Q0;
            Q0=makeQuery(id+"F51.opExtrude","SWEPT_BODY",BODY,{"disambiguationData":[OSD([sQuery(id+"F50.wireOp",EDGE,"E105.bottom"),sQuery(id+"F50.wireOp",EDGE,"E105.top"),sQuery(id+"F50.wireOp",EDGE,"E105.left"),sQuery(id+"F50.wireOp",EDGE,"E105.right")])]});
            transform(context, id + "F54", {"entities" : qUnion([Q0]), "transformType" : TransformType.TRANSLATION_3D, "dx" : 0 * mm, "dy" : 8.5 * mm, "dz" : 0 * mm, "makeCopy" : false});
        }
        {
            var Q0;
            Q0=makeQuery(id+"F53.boolean.opBoolean","COPY",FACE,{"derivedFrom":makeQuery(id+"F53.opExtrude","CAP_FACE",FACE,{"disambiguationData":[OSD([sQuery(id+"F52.wireOp",EDGE,"E108.MirrorCS"),sQuery(id+"F52.wireOp",EDGE,"E109.MirrorCS"),sQuery(id+"F52.wireOp",EDGE,"E110.MirrorCS"),sQuery(id+"F52.wireOp",EDGE,"E111.MirrorCS")])],"isStart":false})});
            var sketch = newSketch(context, id + "F55", { "sketchPlane" : qUnion([Q0])});
            skLineSegment(sketch, "E112.bottom", {"start": v(62.67, -77.71) * mm, "end": v(75.1, -77.71) * mm});
            skLineSegment(sketch, "E112.top", {"start": v(62.67, -81.42) * mm, "end": v(75.1, -81.42) * mm});
            skLineSegment(sketch, "E112.left", {"start": v(62.67, -77.71) * mm, "end": v(62.67, -81.42) * mm});
            skLineSegment(sketch, "E112.right", {"start": v(75.1, -77.71) * mm, "end": v(75.1, -81.42) * mm});
            skLineSegment(sketch, "E113.MirrorCS", {"start": v(-62.67, -77.71) * mm, "end": v(-62.67, -81.42) * mm});
            skLineSegment(sketch, "E114.MirrorCS", {"start": v(-62.67, -77.71) * mm, "end": v(-75.1, -77.71) * mm});
            skLineSegment(sketch, "E115.MirrorCS", {"start": v(-62.67, -81.42) * mm, "end": v(-75.1, -81.42) * mm});
            skLineSegment(sketch, "E116.MirrorCS", {"start": v(-75.1, -77.71) * mm, "end": v(-75.1, -81.42) * mm});
            skCircle(sketch, "E117", {"center": v(50.86, -68.97) * mm, "radius": 4.3 * mm});
            skCircle(sketch, "E118", {"center": v(60.47, -66.72) * mm, "radius": 3.04 * mm});
            skCircle(sketch, "E119.MirrorC", {"center": v(-50.86, -68.97) * mm, "radius": 4.3 * mm});
            skCircle(sketch, "E120.MirrorC", {"center": v(-60.47, -66.72) * mm, "radius": 3.04 * mm});
            skSolve(sketch);
        }
        {
            var Q0;
            Q0 = qSketchRegion(id + "F55", true);
            extrude(context, id + "F56", {"entities" : qUnion([Q0]), "depth" : 12.7 * mm, "offsetDistance" : 25.4 * mm});
        }
        {
            var Q0;
            Q0=makeQuery(id+"F56.opExtrude","CAP_FACE",FACE,{"disambiguationData":[OSD([sQuery(id+"F55.wireOp",EDGE,"E113.MirrorCS"),sQuery(id+"F55.wireOp",EDGE,"E114.MirrorCS"),sQuery(id+"F55.wireOp",EDGE,"E115.MirrorCS"),sQuery(id+"F55.wireOp",EDGE,"E116.MirrorCS")])],"isStart":false});
            var Q1;
            Q1=makeQuery(id+"F56.opExtrude","CAP_EDGE",EDGE,{"disambiguationData":[OSD([sQuery(id+"F55.wireOp",EDGE,"E118")])],"isStart":false});
            var Q2;
            Q2=makeQuery(id+"F56.opExtrude","CAP_FACE",FACE,{"disambiguationData":[OSD([sQuery(id+"F55.wireOp",EDGE,"E117")])],"isStart":false});
            var Q3;
            Q3=makeQuery(id+"F56.opExtrude","CAP_FACE",FACE,{"disambiguationData":[OSD([sQuery(id+"F55.wireOp",EDGE,"E120.MirrorC")])],"isStart":false});
            var Q4;
            Q4=makeQuery(id+"F56.opExtrude","CAP_FACE",FACE,{"disambiguationData":[OSD([sQuery(id+"F55.wireOp",EDGE,"E112.bottom"),sQuery(id+"F55.wireOp",EDGE,"E112.top"),sQuery(id+"F55.wireOp",EDGE,"E112.left"),sQuery(id+"F55.wireOp",EDGE,"E112.right")])],"isStart":false});
            var Q5;
            Q5=makeQuery(id+"F56.opExtrude","CAP_FACE",FACE,{"disambiguationData":[OSD([sQuery(id+"F55.wireOp",EDGE,"E119.MirrorC")])],"isStart":false});
            fillet(context, id + "F57", {"entities" : qUnion([Q0, Q1, Q2, Q3, Q4, Q5]), "radius" : 1.78 * mm, "tangentPropagation" : true, "allowEdgeOverflow" : false});
        }
        {
            var Q0;
            Q0=makeQuery(id+"F1.opExtrude","SWEPT_FACE",FACE,{"disambiguationData":[OSD([sQuery(id+"F0.wireOp",EDGE,"E5")])]});
            var sketch = newSketch(context, id + "F58", { "sketchPlane" : qUnion([Q0])});
            skLineSegment(sketch, "E121.bottom", {"start": v(-78, -63.1) * mm, "end": v(-46.34, -63.1) * mm});
            skLineSegment(sketch, "E121.top", {"start": v(-78, -85.3) * mm, "end": v(-46.34, -85.3) * mm});
            skLineSegment(sketch, "E121.left", {"start": v(-78, -63.1) * mm, "end": v(-78, -85.3) * mm});
            skLineSegment(sketch, "E121.right", {"start": v(-46.34, -63.1) * mm, "end": v(-46.34, -85.3) * mm});
            skLineSegment(sketch, "E122", {"start": v(0, 39.84) * mm, "end": v(0, -43.82) * mm});
            skLineSegment(sketch, "E123.MirrorCS", {"start": v(78, -63.1) * mm, "end": v(78, -85.3) * mm});
            skLineSegment(sketch, "E124.MirrorCS", {"start": v(46.34, -63.1) * mm, "end": v(46.34, -85.3) * mm});
            skLineSegment(sketch, "E125.MirrorCS", {"start": v(78, -63.1) * mm, "end": v(46.34, -63.1) * mm});
            skLineSegment(sketch, "E126.MirrorCS", {"start": v(78, -85.3) * mm, "end": v(46.34, -85.3) * mm});
            skSolve(sketch);
        }
        {
            var Q0;
            Q0 = qSketchRegion(id + "F58", true);
            extrude(context, id + "F59", {"entities" : qUnion([Q0]), "depth" : 0.5 * mm, "offsetDistance" : 25.4 * mm});
        }
        {
            var Q0;
            Q0=makeQuery(id+"F8.boolean.opBoolean","INTERSECT",EDGE,{"derivedFrom":[makeQuery(id+"F3.opShell","OFFSET_FACE",FACE,{"disambiguationData":[OSD([sQuery(id+"F0.wireOp",EDGE,"E3")])]}),makeQuery(id+"F8.opExtrude","SWEPT_FACE",FACE,{"disambiguationData":[OSD([sQuery(id+"F7.wireOp",EDGE,"E20.top")])]})]});
            var Q1;
            {var subQ0=sQuery(id+"F0.wireOp",EDGE,"E15");var subQ1=sQuery(id+"F0.wireOp",EDGE,"E14");var subQ2=sQuery(id+"F0.wireOp",EDGE,"E13");var subQ3=sQuery(id+"F0.wireOp",EDGE,"E12");var subQ4=sQuery(id+"F0.wireOp",EDGE,"E11");var subQ5=sQuery(id+"F0.wireOp",EDGE,"E10");var subQ6=sQuery(id+"F0.wireOp",EDGE,"E5");var subQ7=sQuery(id+"F0.wireOp",EDGE,"E4");var subQ8=sQuery(id+"F0.wireOp",EDGE,"E3");var subQ9=sQuery(id+"F0.wireOp",EDGE,"E2");var subQ10=sQuery(id+"F0.wireOp",EDGE,"E1");var subQ11=sQuery(id+"F0.wireOp",EDGE,"E0");Q1=makeQuery(id+"F6.boolean.opBoolean","INTERSECT",EDGE,{"derivedFrom":[makeQuery(id+"F3.opShell","OFFSET_FACE",FACE,{"disambiguationData":[OSD([subQ11,subQ10,subQ9,subQ8,subQ7,subQ6,subQ5,subQ4,subQ3,subQ2,subQ1,subQ0]),TDD([makeQuery(id+"F1.opExtrude","CAP_FACE",FACE,{"disambiguationData":[OSD([subQ11,subQ10,subQ9,subQ8,subQ7,subQ6,subQ5,subQ4,subQ3,subQ2,subQ1,subQ0])],"isStart":true})])]}),makeQuery(id+"F6.opExtrude","SWEPT_FACE",FACE,{"disambiguationData":[OSD([sQuery(id+"F5.wireOp",EDGE,"E18.top")])]})]});}
            var Q2;
            {var subQ0=sQuery(id+"F0.wireOp",EDGE,"E15");var subQ1=sQuery(id+"F0.wireOp",EDGE,"E14");var subQ2=sQuery(id+"F0.wireOp",EDGE,"E13");var subQ3=sQuery(id+"F0.wireOp",EDGE,"E12");var subQ4=sQuery(id+"F0.wireOp",EDGE,"E11");var subQ5=sQuery(id+"F0.wireOp",EDGE,"E10");var subQ6=sQuery(id+"F0.wireOp",EDGE,"E5");var subQ7=sQuery(id+"F0.wireOp",EDGE,"E4");var subQ8=sQuery(id+"F0.wireOp",EDGE,"E3");var subQ9=sQuery(id+"F0.wireOp",EDGE,"E2");var subQ10=sQuery(id+"F0.wireOp",EDGE,"E1");var subQ11=sQuery(id+"F0.wireOp",EDGE,"E0");Q2=makeQuery(id+"F6.boolean.opBoolean","INTERSECT",EDGE,{"derivedFrom":[makeQuery(id+"F3.opShell","OFFSET_FACE",FACE,{"disambiguationData":[OSD([subQ11,subQ10,subQ9,subQ8,subQ7,subQ6,subQ5,subQ4,subQ3,subQ2,subQ1,subQ0]),TDD([makeQuery(id+"F1.opExtrude","CAP_FACE",FACE,{"disambiguationData":[OSD([subQ11,subQ10,subQ9,subQ8,subQ7,subQ6,subQ5,subQ4,subQ3,subQ2,subQ1,subQ0])],"isStart":false})])]}),makeQuery(id+"F6.opExtrude","SWEPT_FACE",FACE,{"disambiguationData":[OSD([sQuery(id+"F5.wireOp",EDGE,"E18.top")])]})]});}
            var Q3;
            Q3=makeQuery(id+"F8.boolean.opBoolean","INTERSECT",EDGE,{"derivedFrom":[makeQuery(id+"F3.opShell","OFFSET_FACE",FACE,{"disambiguationData":[OSD([sQuery(id+"F0.wireOp",EDGE,"E1")])]}),makeQuery(id+"F8.opExtrude","SWEPT_FACE",FACE,{"disambiguationData":[OSD([sQuery(id+"F7.wireOp",EDGE,"E20.top")])]})]});
            var Q4;
            {var subQ0=sQuery(id+"F0.wireOp",EDGE,"E15");var subQ1=sQuery(id+"F0.wireOp",EDGE,"E14");var subQ2=sQuery(id+"F0.wireOp",EDGE,"E13");var subQ3=sQuery(id+"F0.wireOp",EDGE,"E12");var subQ4=sQuery(id+"F0.wireOp",EDGE,"E11");var subQ5=sQuery(id+"F0.wireOp",EDGE,"E10");var subQ6=sQuery(id+"F0.wireOp",EDGE,"E5");var subQ7=sQuery(id+"F0.wireOp",EDGE,"E4");var subQ8=sQuery(id+"F0.wireOp",EDGE,"E3");var subQ9=sQuery(id+"F0.wireOp",EDGE,"E2");var subQ10=sQuery(id+"F0.wireOp",EDGE,"E1");var subQ11=sQuery(id+"F0.wireOp",EDGE,"E0");Q4=makeQuery(id+"F6.boolean.opBoolean","INTERSECT",EDGE,{"derivedFrom":[makeQuery(id+"F3.opShell","OFFSET_FACE",FACE,{"disambiguationData":[OSD([subQ11,subQ10,subQ9,subQ8,subQ7,subQ6,subQ5,subQ4,subQ3,subQ2,subQ1,subQ0]),TDD([makeQuery(id+"F1.opExtrude","CAP_FACE",FACE,{"disambiguationData":[OSD([subQ11,subQ10,subQ9,subQ8,subQ7,subQ6,subQ5,subQ4,subQ3,subQ2,subQ1,subQ0])],"isStart":false})])]}),makeQuery(id+"F6.opExtrude","SWEPT_FACE",FACE,{"disambiguationData":[OSD([sQuery(id+"F5.wireOp",EDGE,"E19.top")])]})]});}
            var Q5;
            {var subQ0=sQuery(id+"F0.wireOp",EDGE,"E15");var subQ1=sQuery(id+"F0.wireOp",EDGE,"E14");var subQ2=sQuery(id+"F0.wireOp",EDGE,"E13");var subQ3=sQuery(id+"F0.wireOp",EDGE,"E12");var subQ4=sQuery(id+"F0.wireOp",EDGE,"E11");var subQ5=sQuery(id+"F0.wireOp",EDGE,"E10");var subQ6=sQuery(id+"F0.wireOp",EDGE,"E5");var subQ7=sQuery(id+"F0.wireOp",EDGE,"E4");var subQ8=sQuery(id+"F0.wireOp",EDGE,"E3");var subQ9=sQuery(id+"F0.wireOp",EDGE,"E2");var subQ10=sQuery(id+"F0.wireOp",EDGE,"E1");var subQ11=sQuery(id+"F0.wireOp",EDGE,"E0");Q5=makeQuery(id+"F6.boolean.opBoolean","INTERSECT",EDGE,{"derivedFrom":[makeQuery(id+"F3.opShell","OFFSET_FACE",FACE,{"disambiguationData":[OSD([subQ11,subQ10,subQ9,subQ8,subQ7,subQ6,subQ5,subQ4,subQ3,subQ2,subQ1,subQ0]),TDD([makeQuery(id+"F1.opExtrude","CAP_FACE",FACE,{"disambiguationData":[OSD([subQ11,subQ10,subQ9,subQ8,subQ7,subQ6,subQ5,subQ4,subQ3,subQ2,subQ1,subQ0])],"isStart":true})])]}),makeQuery(id+"F6.opExtrude","SWEPT_FACE",FACE,{"disambiguationData":[OSD([sQuery(id+"F5.wireOp",EDGE,"E19.top")])]})]});}
            fillet(context, id + "F60", {"entities" : qUnion([Q0, Q1, Q2, Q3, Q4, Q5]), "radius" : 2.54 * mm, "tangentPropagation" : true, "allowEdgeOverflow" : false});
        }
    });
